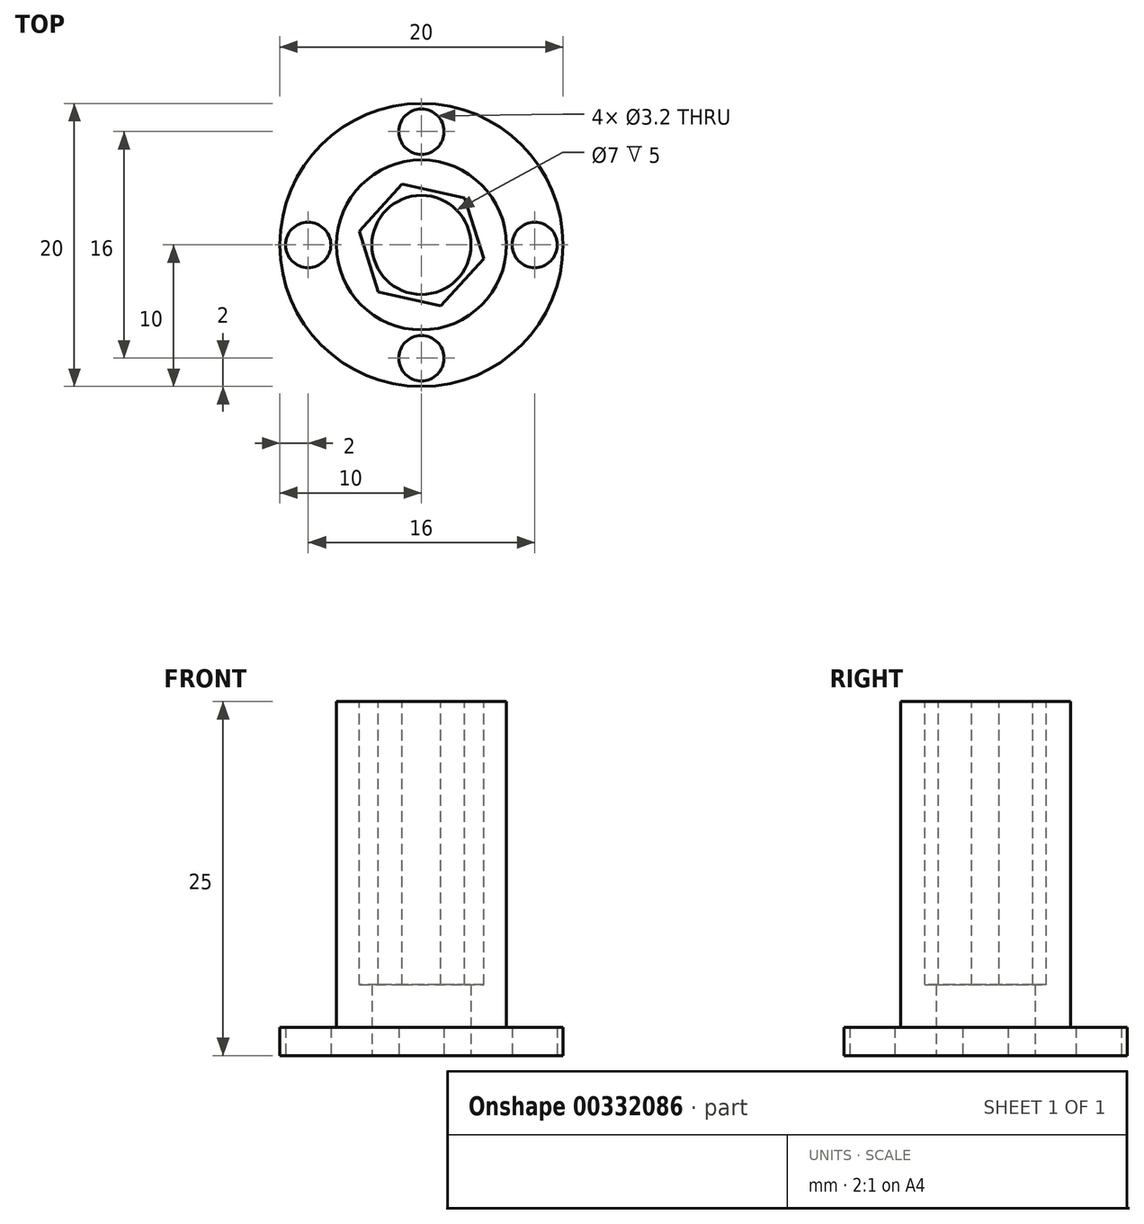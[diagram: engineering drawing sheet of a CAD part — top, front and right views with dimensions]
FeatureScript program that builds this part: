
annotation { "Feature Type Name" : "Feature", "Feature Type Description" : "" }
export const myFeature = defineFeature(function(context is Context, id is Id, definition is map)
    precondition{}
    {
        {
            var Q0;
            Q0=qCreatedBy(makeId("Top.planeOp"),FACE);
            var sketch = newSketch(context, id + "F0", { "sketchPlane" : qUnion([Q0])});
            skCircle(sketch, "E0", {"center": v(0, 0) * mm, "radius": 10 * mm});
            skCircle(sketch, "E1", {"center": v(0, 0) * mm, "radius": 8 * mm, "construction": true});
            skPoint(sketch, "E2", {"position": v(0, 8) * mm});
            skPoint(sketch, "E3", {"position": v(0, -8) * mm});
            skPoint(sketch, "E4", {"position": v(8, 0) * mm});
            skPoint(sketch, "E5", {"position": v(-8, 0) * mm});
            skCircle(sketch, "E6", {"center": v(0, 0) * mm, "radius": 6 * mm});
            skCircle(sketch, "E7", {"center": v(0, 0) * mm, "radius": 3.5 * mm});
            skSolve(sketch);
        }
        {
            var Q0;
            Q0=makeQuery(id+"F0.imprint","IMPRINT",FACE,{"disambiguationData":[TD([[makeQuery(id+"F0.imprint","IMPRINT",EDGE,{"derivedFrom":sQuery(id+"F0.wireOp",EDGE,"E0")}),1.0]])]});
            extrude(context, id + "F1", {"entities" : qUnion([Q0]), "depth" : 2 * mm});
        }
        {
            var Q0;
            Q0=makeQuery(id+"F0.imprint","IMPRINT",FACE,{"disambiguationData":[TD([[makeQuery(id+"F0.imprint","IMPRINT",EDGE,{"derivedFrom":sQuery(id+"F0.wireOp",EDGE,"E6")}),1.0]])]});
            extrude(context, id + "F2", {"entities" : qUnion([Q0]), "operationType" : NewBodyOperationType.ADD, "depth" : 25 * mm});
        }
        {
            var Q0;
            Q0=makeQuery(id+"F2.opExtrude","CAP_FACE",FACE,{"disambiguationData":[OSD([sQuery(id+"F0.wireOp",EDGE,"E6")])],"isStart":false});
            var sketch = newSketch(context, id + "F3", { "sketchPlane" : qUnion([Q0])});
            skCircle(sketch, "E8.cCircle", {"center": v(0, 0) * mm, "radius": 3.9 * mm, "construction": true});
            skLineSegment(sketch, "E8.0", {"start": v(4.4, -0.97) * mm, "end": v(1.36, -4.3) * mm});
            skLineSegment(sketch, "E8.1", {"start": v(1.36, -4.3) * mm, "end": v(-3.04, -3.33) * mm});
            skLineSegment(sketch, "E8.2", {"start": v(-3.04, -3.33) * mm, "end": v(-4.4, 0.97) * mm});
            skLineSegment(sketch, "E8.3", {"start": v(-4.4, 0.97) * mm, "end": v(-1.36, 4.3) * mm});
            skLineSegment(sketch, "E8.4", {"start": v(-1.36, 4.3) * mm, "end": v(3.04, 3.33) * mm});
            skLineSegment(sketch, "E8.5", {"start": v(3.04, 3.33) * mm, "end": v(4.4, -0.97) * mm});
            skPoint(sketch, "E8.0.midPoint", {"position": v(2.88, -2.63) * mm});
            skSolve(sketch);
        }
        {
            var Q0;
            Q0=makeQuery(id+"F3.imprint","IMPRINT",FACE,{"disambiguationData":[TD([[makeQuery(id+"F3.imprint","IMPRINT",EDGE,{"derivedFrom":sQuery(id+"F3.wireOp",EDGE,"E8.0")}),-1.0]])]});
            extrude(context, id + "F4", {"entities" : qUnion([Q0]), "operationType" : NewBodyOperationType.REMOVE, "oppositeDirection" : true, "depth" : 20 * mm});
        }
        {
            var Q0;
            Q0=sQuery(id+"F0.wireOp",VERTEX,"E5");
            var Q1;
            Q1=sQuery(id+"F0.wireOp",VERTEX,"E2");
            var Q2;
            Q2=sQuery(id+"F0.wireOp",VERTEX,"E4");
            var Q3;
            Q3=sQuery(id+"F0.wireOp",VERTEX,"E3");
            var Q4;
            Q4=makeQuery(id+"F1.opExtrude","SWEPT_BODY",BODY,{"disambiguationData":[OSD([sQuery(id+"F0.wireOp",EDGE,"E0"),sQuery(id+"F0.wireOp",EDGE,"E6")])]});
            hole(context, id + "F5", {"style" : HoleStyle.SIMPLE, "endStyle" : HoleEndStyle.THROUGH, "oppositeDirection" : true, "holeDiameter" : 3.2 * mm, "tappedDepth" : 12 * mm, "tapClearance" : 3, "locations" : qUnion([Q0, Q1, Q2, Q3]), "scope" : qUnion([Q4])});
        }
    });
